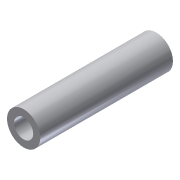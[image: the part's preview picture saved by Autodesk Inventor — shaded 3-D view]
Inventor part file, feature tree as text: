
AUTODESK INVENTOR PART (.ipt)
format: ipt  version: 2013 (Build 170138000, 138)  size: 74,240 bytes
history: native  units: in
note: dims shown in document units (in); Inventor stores cm internally (conversion verified against a paired STEP export)
features: extrude x1, sketch x1
ambient origin geometry x8: Origin, YZ Plane, XZ Plane, XY Plane, X Axis, Y Axis, Z Axis, Center Point
bodies: Solid1 (feature_tree)
feature tree (2):
  extrude  "Extrusion1"  Depth=2.0in TaperAngle=0.0deg
  sketch  "Sketch1"  dims[d0=0.5in d1=2.0in d2=0.0in]
